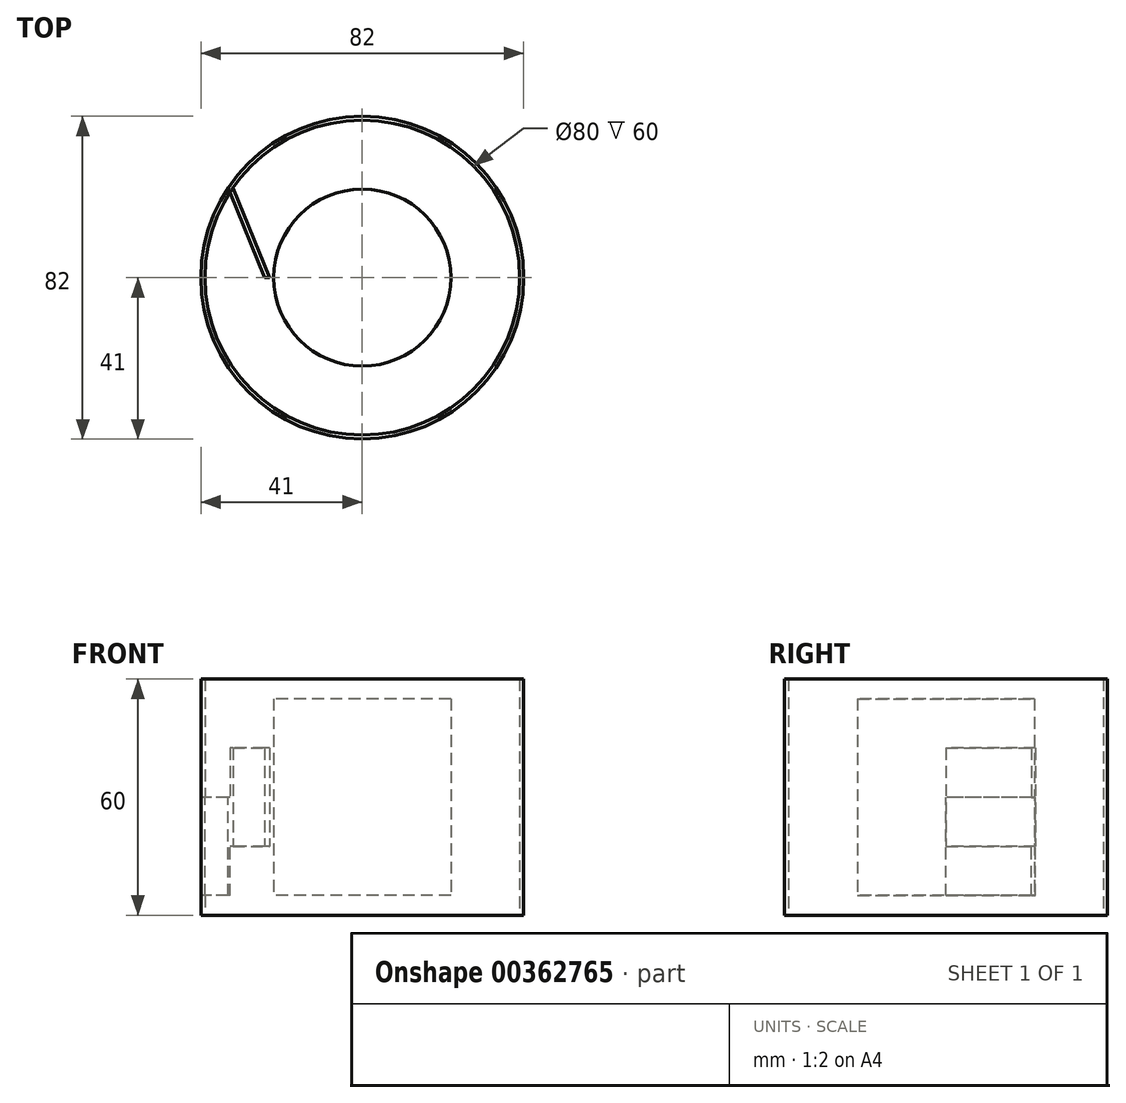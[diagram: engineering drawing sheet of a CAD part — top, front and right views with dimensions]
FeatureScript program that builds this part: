
annotation { "Feature Type Name" : "Feature", "Feature Type Description" : "" }
export const myFeature = defineFeature(function(context is Context, id is Id, definition is map)
    precondition{}
    {
        {
            var Q0;
            Q0=qCreatedBy(makeId("Top.planeOp"),FACE);
            var sketch = newSketch(context, id + "F0", { "sketchPlane" : qUnion([Q0])});
            skCircle(sketch, "E0", {"center": v(0, 0) * mm, "radius": 22.5 * mm});
            skCircle(sketch, "E1", {"center": v(0, 0) * mm, "radius": 40 * mm});
            skCircle(sketch, "E2", {"center": v(0, 0) * mm, "radius": 41 * mm});
            skSolve(sketch);
        }
        {
            var Q0;
            Q0=makeQuery(id+"F0.imprint","IMPRINT",FACE,{"disambiguationData":[TD([[makeQuery(id+"F0.imprint","IMPRINT",EDGE,{"derivedFrom":sQuery(id+"F0.wireOp",EDGE,"E0")}),1.0]])]});
            extrude(context, id + "F1", {"entities" : qUnion([Q0]), "endBound" : BoundingType.SYMMETRIC, "depth" : 50 * mm});
        }
        {
            var Q0;
            Q0=makeQuery(id+"F0.imprint","IMPRINT",FACE,{"disambiguationData":[TD([[makeQuery(id+"F0.imprint","IMPRINT",EDGE,{"derivedFrom":sQuery(id+"F0.wireOp",EDGE,"E1")}),-1.0]])]});
            extrude(context, id + "F2", {"entities" : qUnion([Q0]), "endBound" : BoundingType.SYMMETRIC, "depth" : 60 * mm});
        }
        {
            var Q0;
            Q0=qCreatedBy(makeId("Top.planeOp"),FACE);
            var sketch = newSketch(context, id + "F3", { "sketchPlane" : qUnion([Q0])});
            skArc(sketch, "E3.0", {"start": v(-33.63, 21.66) * mm, "mid": v(33.26, -22.22) * mm, "end": v(-32.88, 22.78) * mm});
            skCircle(sketch, "E4.0", {"center": v(0, 0) * mm, "radius": 41 * mm});
            skLineSegment(sketch, "E5", {"start": v(-32.88, 22.78) * mm, "end": v(-23.6, 0) * mm});
            skLineSegment(sketch, "E6", {"start": v(-23.6, 0) * mm, "end": v(-24.8, 0) * mm});
            skLineSegment(sketch, "E7", {"start": v(-24.8, 0) * mm, "end": v(-33.63, 21.66) * mm});
            skLineSegment(sketch, "E8", {"start": v(-33.63, 21.66) * mm, "end": v(-34.1, 22.78) * mm});
            skLineSegment(sketch, "E9", {"start": v(-40, 0) * mm, "end": v(-41, 0) * mm});
            skArc(sketch, "E10", {"start": v(-41, 0) * mm, "mid": v(-39.23, 11.9) * mm, "end": v(-34.1, 22.78) * mm});
            skArc(sketch, "E11", {"start": v(-40, 0) * mm, "mid": v(-38.37, 11.29) * mm, "end": v(-33.63, 21.66) * mm});
            skLineSegment(sketch, "E12", {"start": v(-34.1, 22.78) * mm, "end": v(-32.88, 22.78) * mm});
            skSolve(sketch);
        }
        {
            var Q0;
            Q0=makeQuery(id+"F3.imprint","IMPRINT",FACE,{"disambiguationData":[TD([[makeQuery(id+"F3.imprint","IMPRINT",EDGE,{"derivedFrom":sQuery(id+"F3.wireOp",EDGE,"E5")}),-1.0]])]});
            extrude(context, id + "F4", {"entities" : qUnion([Q0]), "operationType" : NewBodyOperationType.ADD, "endBound" : BoundingType.SYMMETRIC, "depth" : 25 * mm});
        }
        {
            var Q0;
            {var subQ0=sQuery(id+"F3.wireOp",EDGE,"E8");Q0=makeQuery(id+"F3.imprint","IMPRINT",FACE,{"disambiguationData":[TD([[makeQuery(id+"F3.imprint","IMPRINT",EDGE,{"derivedFrom":subQ0}),1.0]])]});}
            extrude(context, id + "F5", {"entities" : qUnion([Q0]), "operationType" : NewBodyOperationType.REMOVE, "oppositeDirection" : true, "depth" : 25 * mm});
        }
    });
